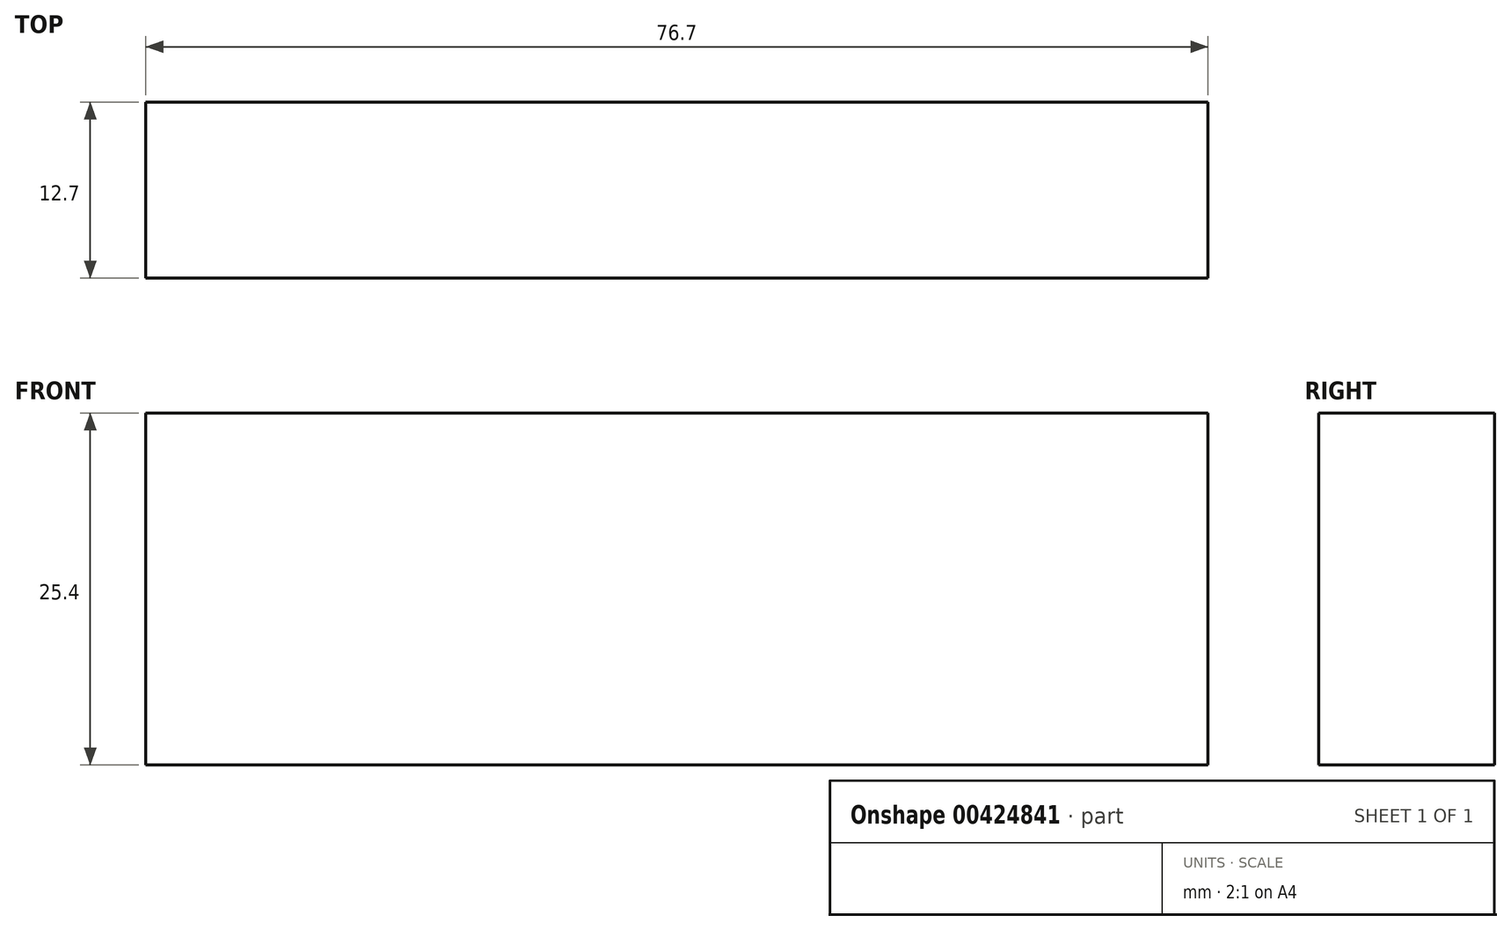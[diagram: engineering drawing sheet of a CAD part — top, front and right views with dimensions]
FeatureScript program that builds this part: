
annotation { "Feature Type Name" : "Feature", "Feature Type Description" : "" }
export const myFeature = defineFeature(function(context is Context, id is Id, definition is map)
    precondition{}
    {
        {
            var Q0;
            Q0=qCreatedBy(makeId("Front.planeOp"),FACE);
            var sketch = newSketch(context, id + "F0", { "sketchPlane" : qUnion([Q0])});
            skLineSegment(sketch, "E0", {"start": v(0, 0) * mm, "end": v(0, 25.4) * mm});
            skLineSegment(sketch, "E1", {"start": v(0, 25.4) * mm, "end": v(76.7, 25.4) * mm});
            skLineSegment(sketch, "E2", {"start": v(76.7, 25.4) * mm, "end": v(76.7, 0) * mm});
            skLineSegment(sketch, "E3", {"start": v(0, 0) * mm, "end": v(76.7, 0) * mm});
            skSolve(sketch);
        }
        {
            var Q0;
            Q0=makeQuery(id+"F0.imprint","IMPRINT",FACE,{"disambiguationData":[TD([[makeQuery(id+"F0.imprint","IMPRINT",EDGE,{"derivedFrom":sQuery(id+"F0.wireOp",EDGE,"E0")}),-1.0]])]});
            extrude(context, id + "F1", {"entities" : qUnion([Q0]), "depth" : 12.7 * mm});
        }
    });
